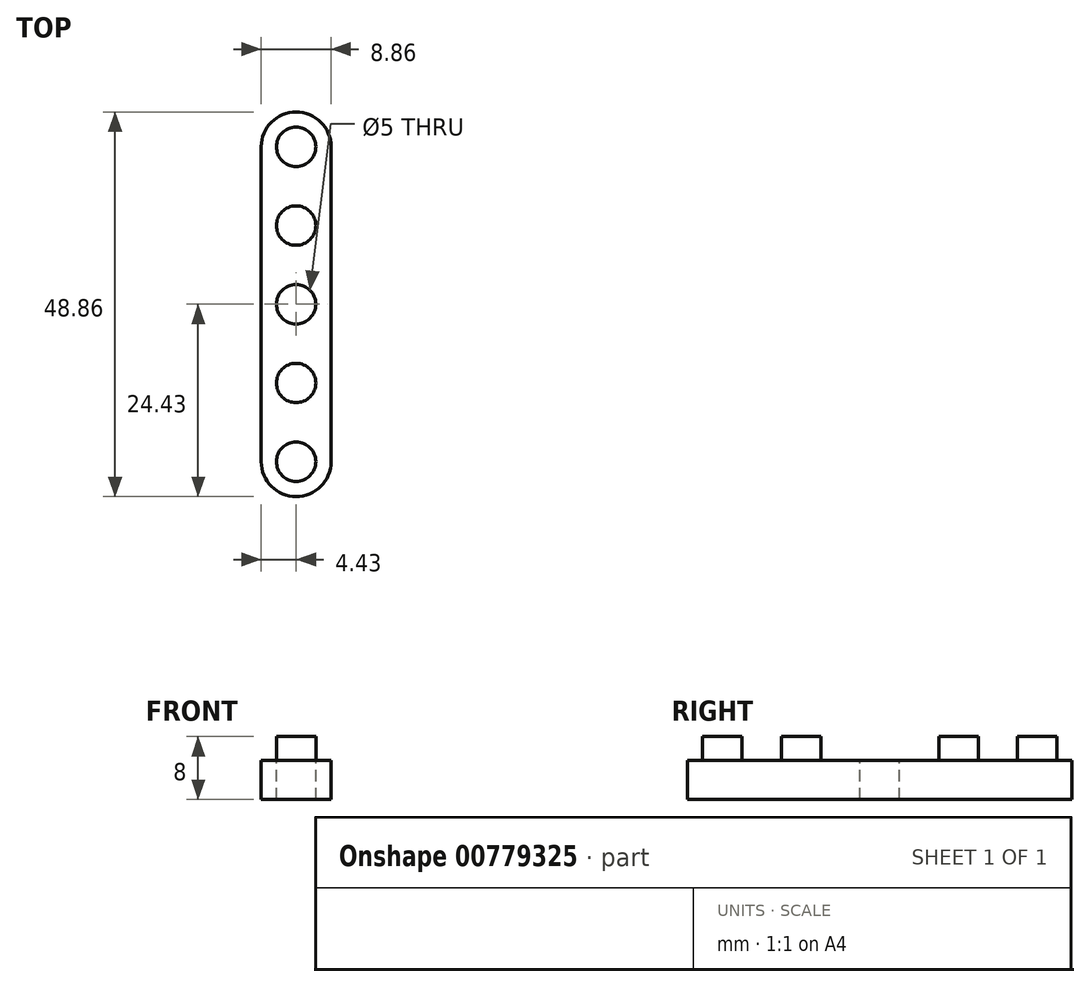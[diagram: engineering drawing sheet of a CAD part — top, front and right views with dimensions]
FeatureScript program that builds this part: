
annotation { "Feature Type Name" : "Feature", "Feature Type Description" : "" }
export const myFeature = defineFeature(function(context is Context, id is Id, definition is map)
    precondition{}
    {
        {
            var Q0;
            Q0=qCreatedBy(makeId("Top.planeOp"),FACE);
            var sketch = newSketch(context, id + "F0", { "sketchPlane" : qUnion([Q0])});
            skLineSegment(sketch, "E0.left", {"start": v(-4.43, 20) * mm, "end": v(-4.43, -20) * mm});
            skLineSegment(sketch, "E0.right", {"start": v(4.43, 20) * mm, "end": v(4.43, -20) * mm});
            skPoint(sketch, "E0.middle", {"position": v(0, 0) * mm});
            skArc(sketch, "E1", {"start": v(-4.43, 20) * mm, "mid": v(0, 24.43) * mm, "end": v(4.43, 20) * mm});
            skArc(sketch, "E2", {"start": v(-4.43, -20) * mm, "mid": v(0, -24.43) * mm, "end": v(4.43, -20) * mm});
            skCircle(sketch, "E3", {"center": v(0, 0) * mm, "radius": 2.5 * mm});
            skSolve(sketch);
        }
        {
            var Q0;
            Q0=makeQuery(id+"F0.imprint","IMPRINT",FACE,{"disambiguationData":[TD([[makeQuery(id+"F0.imprint","IMPRINT",EDGE,{"derivedFrom":sQuery(id+"F0.wireOp",EDGE,"E0.left")}),1.0]])]});
            var sketch = newSketch(context, id + "F1", { "sketchPlane" : qUnion([Q0])});
            skSolve(sketch);
        }
        {
            var Q0;
            Q0=makeQuery(id+"F0.imprint","IMPRINT",FACE,{"disambiguationData":[TD([[makeQuery(id+"F0.imprint","IMPRINT",EDGE,{"derivedFrom":sQuery(id+"F0.wireOp",EDGE,"E0.left")}),1.0]])]});
            var Q1;
            Q1=makeQuery(id+"F0.imprint","IMPRINT",FACE,{"disambiguationData":[TD([[makeQuery(id+"F0.imprint","IMPRINT",EDGE,{"derivedFrom":sQuery(id+"F0.wireOp",EDGE,"E3")}),1.0]])]});
            var Q2;
            Q2=makeQuery(id+"F1.imprint","IMPRINT",FACE,{"disambiguationData":[TD([[makeQuery(id+"F1.imprint","IMPRINT",EDGE,{"derivedFrom":makeQuery(id+"F0.imprint","IMPRINT",EDGE,{"derivedFrom":sQuery(id+"F0.wireOp",EDGE,"E0.left")})}),1.0]])]});
            extrude(context, id + "F2", {"entities" : qUnion([Q0, Q1, Q2]), "oppositeDirection" : true, "depth" : 5 * mm, "offsetDistance" : 25.4 * mm});
        }
        {
            var Q0;
            Q0=makeQuery(id+"F2.opExtrude","CAP_FACE",FACE,{"disambiguationData":[OSD([sQuery(id+"F0.wireOp",EDGE,"E0.left"),sQuery(id+"F0.wireOp",EDGE,"E0.right"),sQuery(id+"F0.wireOp",EDGE,"E1"),sQuery(id+"F0.wireOp",EDGE,"E2")])],"isStart":true});
            var sketch = newSketch(context, id + "F3", { "sketchPlane" : qUnion([Q0])});
            skCircle(sketch, "E4", {"center": v(0, 20) * mm, "radius": 2.5 * mm});
            skCircle(sketch, "E5", {"center": v(0, 10) * mm, "radius": 2.5 * mm});
            skCircle(sketch, "E6", {"center": v(0, -10) * mm, "radius": 2.5 * mm});
            skCircle(sketch, "E7", {"center": v(0, -20) * mm, "radius": 2.5 * mm});
            skSolve(sketch);
        }
        {
            var Q0;
            Q0=makeQuery(id+"F3.imprint","IMPRINT",FACE,{"disambiguationData":[TD([[makeQuery(id+"F3.imprint","IMPRINT",EDGE,{"derivedFrom":sQuery(id+"F3.wireOp",EDGE,"E5")}),1.0]])]});
            var Q1;
            Q1=makeQuery(id+"F3.imprint","IMPRINT",FACE,{"disambiguationData":[TD([[makeQuery(id+"F3.imprint","IMPRINT",EDGE,{"derivedFrom":sQuery(id+"F3.wireOp",EDGE,"E4")}),1.0]])]});
            var Q2;
            Q2=makeQuery(id+"F3.imprint","IMPRINT",FACE,{"disambiguationData":[TD([[makeQuery(id+"F3.imprint","IMPRINT",EDGE,{"derivedFrom":sQuery(id+"F3.wireOp",EDGE,"E6")}),1.0]])]});
            var Q3;
            Q3=makeQuery(id+"F3.imprint","IMPRINT",FACE,{"disambiguationData":[TD([[makeQuery(id+"F3.imprint","IMPRINT",EDGE,{"derivedFrom":sQuery(id+"F3.wireOp",EDGE,"E7")}),1.0]])]});
            extrude(context, id + "F4", {"entities" : qUnion([Q0, Q1, Q2, Q3]), "depth" : 3 * mm, "offsetDistance" : 25.4 * mm});
        }
        {
            var Q0;
            Q0=makeQuery(id+"F2.opExtrude","CAP_FACE",FACE,{"disambiguationData":[OSD([sQuery(id+"F0.wireOp",EDGE,"E0.left"),sQuery(id+"F0.wireOp",EDGE,"E0.right"),sQuery(id+"F0.wireOp",EDGE,"E1"),sQuery(id+"F0.wireOp",EDGE,"E2")])],"isStart":true});
            var sketch = newSketch(context, id + "F5", { "sketchPlane" : qUnion([Q0])});
            skCircle(sketch, "E8", {"center": v(0, 0) * mm, "radius": 2.5 * mm});
            skSolve(sketch);
        }
        {
            var Q0;
            Q0 = qSketchRegion(id + "F5", true);
            extrude(context, id + "F6", {"entities" : qUnion([Q0]), "operationType" : NewBodyOperationType.REMOVE, "endBound" : BoundingType.THROUGH_ALL, "oppositeDirection" : true, "depth" : 25.4 * mm, "offsetDistance" : 25.4 * mm});
        }
    });
